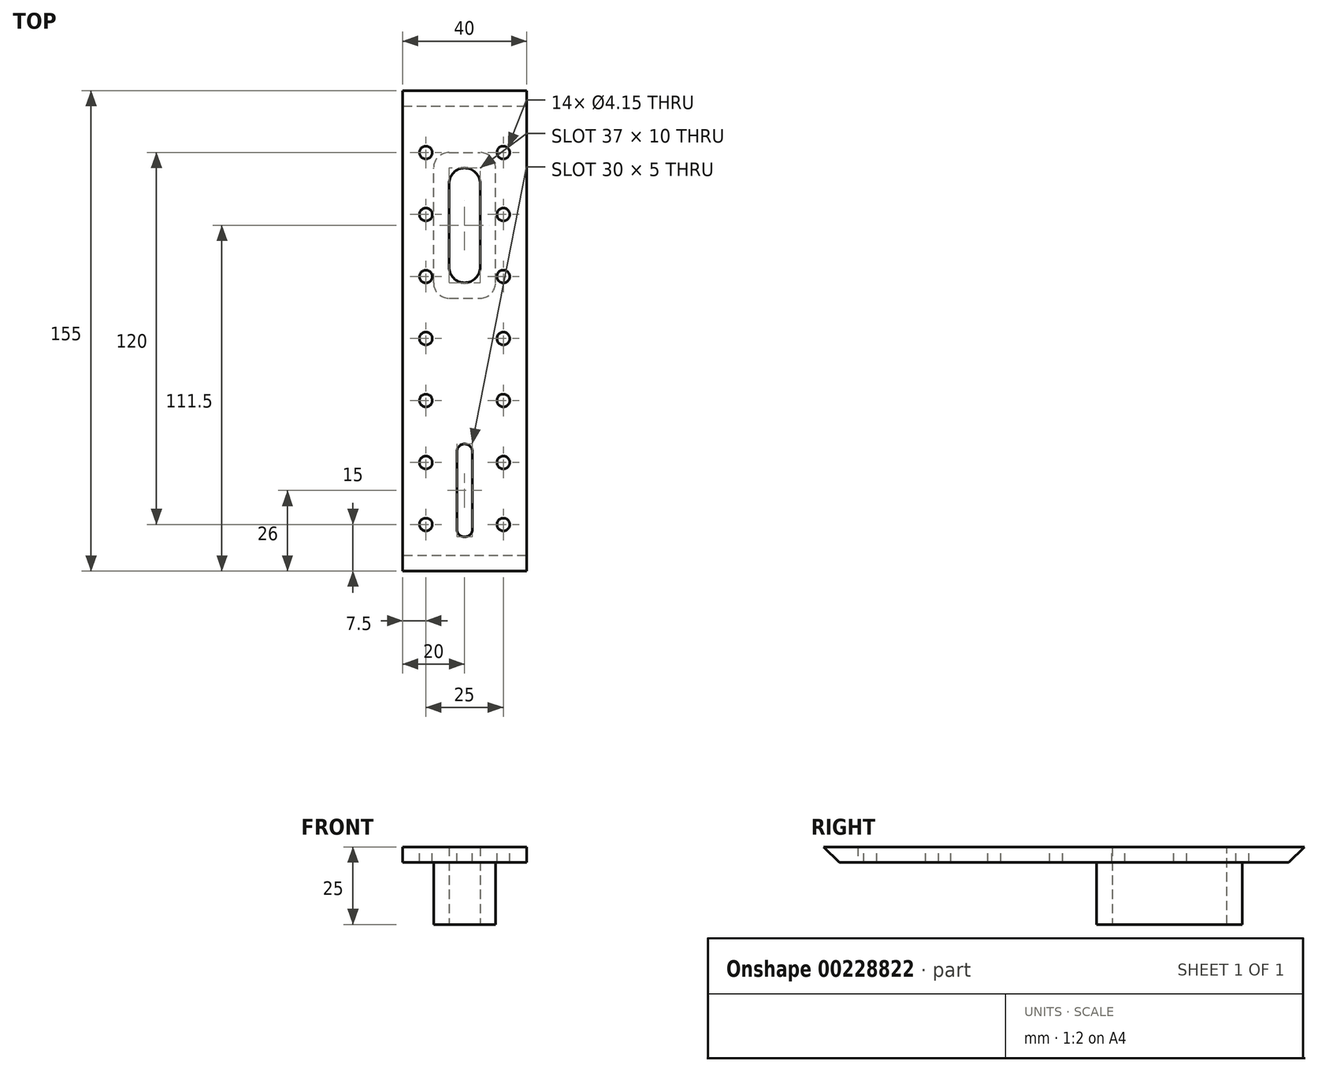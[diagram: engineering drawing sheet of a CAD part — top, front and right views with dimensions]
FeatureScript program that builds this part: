
annotation { "Feature Type Name" : "Feature", "Feature Type Description" : "" }
export const myFeature = defineFeature(function(context is Context, id is Id, definition is map)
    precondition{}
    {
        {
            var Q0;
            Q0=qCreatedBy(makeId("Top.planeOp"),FACE);
            var sketch = newSketch(context, id + "F0", { "sketchPlane" : qUnion([Q0])});
            skLineSegment(sketch, "E0.bottom", {"start": v(-20, 97.5) * mm, "end": v(20, 97.5) * mm});
            skLineSegment(sketch, "E0.top", {"start": v(-20, -57.5) * mm, "end": v(20, -57.5) * mm});
            skLineSegment(sketch, "E0.left", {"start": v(-20, 97.5) * mm, "end": v(-20, -57.5) * mm});
            skLineSegment(sketch, "E0.right", {"start": v(20, 97.5) * mm, "end": v(20, -57.5) * mm});
            skLineSegment(sketch, "E1.bottom", {"start": v(-5, 72.5) * mm, "end": v(5, 72.5) * mm});
            skLineSegment(sketch, "E1.top", {"start": v(-5, 35.5) * mm, "end": v(5, 35.5) * mm});
            skLineSegment(sketch, "E1.left", {"start": v(-5, 72.5) * mm, "end": v(-5, 35.5) * mm});
            skLineSegment(sketch, "E1.right", {"start": v(5, 72.5) * mm, "end": v(5, 35.5) * mm});
            skSolve(sketch);
        }
        {
            var Q0;
            Q0=makeQuery(id+"F0.imprint","IMPRINT",FACE,{"disambiguationData":[TD([[makeQuery(id+"F0.imprint","IMPRINT",EDGE,{"derivedFrom":sQuery(id+"F0.wireOp",EDGE,"E0.bottom")}),-1.0]])]});
            extrude(context, id + "F1", {"entities" : qUnion([Q0]), "depth" : 5 * mm});
        }
        {
            var Q0;
            Q0=makeQuery(id+"F1.opExtrude","SWEPT_EDGE",EDGE,{"disambiguationData":[OSD([sQuery(id+"F0.wireOp",EDGE,"E1.bottom"),sQuery(id+"F0.wireOp",EDGE,"E1.right")])]});
            var Q1;
            Q1=makeQuery(id+"F1.opExtrude","SWEPT_EDGE",EDGE,{"disambiguationData":[OSD([sQuery(id+"F0.wireOp",EDGE,"E1.bottom"),sQuery(id+"F0.wireOp",EDGE,"E1.left")])]});
            var Q2;
            Q2=makeQuery(id+"F1.opExtrude","SWEPT_EDGE",EDGE,{"disambiguationData":[OSD([sQuery(id+"F0.wireOp",EDGE,"E1.top"),sQuery(id+"F0.wireOp",EDGE,"E1.right")])]});
            var Q3;
            Q3=makeQuery(id+"F1.opExtrude","SWEPT_EDGE",EDGE,{"disambiguationData":[OSD([sQuery(id+"F0.wireOp",EDGE,"E1.top"),sQuery(id+"F0.wireOp",EDGE,"E1.left")])]});
            fillet(context, id + "F2", {"entities" : qUnion([Q0, Q1, Q2, Q3]), "radius" : 5 * mm, "tangentPropagation" : true, "allowEdgeOverflow" : false});
        }
        {
            var Q0;
            Q0=makeQuery(id+"F1.opExtrude","CAP_FACE",FACE,{"disambiguationData":[OSD([sQuery(id+"F0.wireOp",EDGE,"E0.bottom"),sQuery(id+"F0.wireOp",EDGE,"E0.top"),sQuery(id+"F0.wireOp",EDGE,"E0.left"),sQuery(id+"F0.wireOp",EDGE,"E0.right"),sQuery(id+"F0.wireOp",EDGE,"E1.bottom"),sQuery(id+"F0.wireOp",EDGE,"E1.top"),sQuery(id+"F0.wireOp",EDGE,"E1.left"),sQuery(id+"F0.wireOp",EDGE,"E1.right")])],"isStart":true});
            var sketch = newSketch(context, id + "F3", { "sketchPlane" : qUnion([Q0])});
            skLineSegment(sketch, "E2.bottom", {"start": v(-10, -30.5) * mm, "end": v(10, -30.5) * mm});
            skLineSegment(sketch, "E2.top", {"start": v(-10, -77.5) * mm, "end": v(10, -77.5) * mm});
            skLineSegment(sketch, "E2.left", {"start": v(-10, -30.5) * mm, "end": v(-10, -77.5) * mm});
            skLineSegment(sketch, "E2.right", {"start": v(10, -30.5) * mm, "end": v(10, -77.5) * mm});
            skSolve(sketch);
        }
        {
            var Q0;
            Q0=makeQuery(id+"F3.imprint","IMPRINT",FACE,{"disambiguationData":[TD([[makeQuery(id+"F3.imprint","IMPRINT",EDGE,{"derivedFrom":sQuery(id+"F3.wireOp",EDGE,"E2.bottom")}),-1.0]])]});
            extrude(context, id + "F4", {"entities" : qUnion([Q0]), "operationType" : NewBodyOperationType.ADD, "depth" : 20 * mm});
        }
        {
            var Q0;
            Q0=makeQuery(id+"F4.opExtrude","SWEPT_EDGE",EDGE,{"disambiguationData":[OSD([sQuery(id+"F3.wireOp",EDGE,"E2.bottom"),sQuery(id+"F3.wireOp",EDGE,"E2.left")])]});
            var Q1;
            Q1=makeQuery(id+"F4.opExtrude","SWEPT_EDGE",EDGE,{"disambiguationData":[OSD([sQuery(id+"F3.wireOp",EDGE,"E2.bottom"),sQuery(id+"F3.wireOp",EDGE,"E2.right")])]});
            var Q2;
            Q2=makeQuery(id+"F4.opExtrude","SWEPT_EDGE",EDGE,{"disambiguationData":[OSD([sQuery(id+"F3.wireOp",EDGE,"E2.top"),sQuery(id+"F3.wireOp",EDGE,"E2.left")])]});
            var Q3;
            Q3=makeQuery(id+"F4.opExtrude","SWEPT_EDGE",EDGE,{"disambiguationData":[OSD([sQuery(id+"F3.wireOp",EDGE,"E2.top"),sQuery(id+"F3.wireOp",EDGE,"E2.right")])]});
            fillet(context, id + "F5", {"entities" : qUnion([Q0, Q1, Q2, Q3]), "radius" : 5 * mm, "tangentPropagation" : true, "allowEdgeOverflow" : false});
        }
        {
            var Q0;
            Q0=makeQuery(id+"F1.opExtrude","CAP_EDGE",EDGE,{"disambiguationData":[OSD([sQuery(id+"F0.wireOp",EDGE,"E0.bottom")])],"isStart":true});
            var Q1;
            Q1=makeQuery(id+"F1.opExtrude","CAP_EDGE",EDGE,{"disambiguationData":[OSD([sQuery(id+"F0.wireOp",EDGE,"E0.top")])],"isStart":true});
            chamfer(context, id + "F6", {"entities" : qUnion([Q0, Q1]), "width" : 5 * mm, "tangentPropagation" : true});
        }
        {
            var Q0;
            Q0=makeQuery(id+"F1.opExtrude","CAP_FACE",FACE,{"disambiguationData":[OSD([sQuery(id+"F0.wireOp",EDGE,"E0.bottom"),sQuery(id+"F0.wireOp",EDGE,"E0.top"),sQuery(id+"F0.wireOp",EDGE,"E0.left"),sQuery(id+"F0.wireOp",EDGE,"E0.right"),sQuery(id+"F0.wireOp",EDGE,"E1.bottom"),sQuery(id+"F0.wireOp",EDGE,"E1.top"),sQuery(id+"F0.wireOp",EDGE,"E1.left"),sQuery(id+"F0.wireOp",EDGE,"E1.right")])],"isStart":false});
            var sketch = newSketch(context, id + "F7", { "sketchPlane" : qUnion([Q0])});
            skCircle(sketch, "E3", {"center": v(-12.5, -42.5) * mm, "radius": 2.07 * mm});
            skCircle(sketch, "E4.0.1.0", {"center": v(-12.5, -22.5) * mm, "radius": 2.07 * mm});
            skCircle(sketch, "E4.0.2.0", {"center": v(-12.5, -2.5) * mm, "radius": 2.07 * mm});
            skCircle(sketch, "E4.0.3.0", {"center": v(-12.5, 17.5) * mm, "radius": 2.07 * mm});
            skCircle(sketch, "E4.0.4.0", {"center": v(-12.5, 37.5) * mm, "radius": 2.07 * mm});
            skCircle(sketch, "E4.1.0.0", {"center": v(12.5, -42.5) * mm, "radius": 2.07 * mm});
            skCircle(sketch, "E4.1.1.0", {"center": v(12.5, -22.5) * mm, "radius": 2.07 * mm});
            skCircle(sketch, "E4.1.2.0", {"center": v(12.5, -2.5) * mm, "radius": 2.07 * mm});
            skCircle(sketch, "E4.1.3.0", {"center": v(12.5, 17.5) * mm, "radius": 2.07 * mm});
            skCircle(sketch, "E4.1.4.0", {"center": v(12.5, 37.5) * mm, "radius": 2.07 * mm});
            skLineSegment(sketch, "E4.direction1", {"start": v(-12.5, -42.5) * mm, "end": v(12.5, -42.5) * mm, "construction": true});
            skLineSegment(sketch, "E4.direction2", {"start": v(-12.5, -42.5) * mm, "end": v(-12.5, -22.5) * mm, "construction": true});
            skCircle(sketch, "E5.0.0.5", {"center": v(-12.5, 57.5) * mm, "radius": 2.07 * mm});
            skCircle(sketch, "E5.0.0.6", {"center": v(-12.5, 77.5) * mm, "radius": 2.07 * mm});
            skCircle(sketch, "E5.0.1.5", {"center": v(12.5, 57.5) * mm, "radius": 2.07 * mm});
            skCircle(sketch, "E5.0.1.6", {"center": v(12.5, 77.5) * mm, "radius": 2.07 * mm});
            skSolve(sketch);
        }
        {
            var Q0;
            Q0=makeQuery(id+"F7.imprint","IMPRINT",FACE,{"disambiguationData":[TD([[makeQuery(id+"F7.imprint","IMPRINT",EDGE,{"derivedFrom":sQuery(id+"F7.wireOp",EDGE,"E3")}),1.0]])]});
            var Q1;
            Q1=makeQuery(id+"F7.imprint","IMPRINT",FACE,{"disambiguationData":[TD([[makeQuery(id+"F7.imprint","IMPRINT",EDGE,{"derivedFrom":sQuery(id+"F7.wireOp",EDGE,"E4.1.0.0")}),1.0]])]});
            var Q2;
            Q2=makeQuery(id+"F7.imprint","IMPRINT",FACE,{"disambiguationData":[TD([[makeQuery(id+"F7.imprint","IMPRINT",EDGE,{"derivedFrom":sQuery(id+"F7.wireOp",EDGE,"E4.0.1.0")}),1.0]])]});
            var Q3;
            Q3=makeQuery(id+"F7.imprint","IMPRINT",FACE,{"disambiguationData":[TD([[makeQuery(id+"F7.imprint","IMPRINT",EDGE,{"derivedFrom":sQuery(id+"F7.wireOp",EDGE,"E4.1.1.0")}),1.0]])]});
            var Q4;
            Q4=makeQuery(id+"F7.imprint","IMPRINT",FACE,{"disambiguationData":[TD([[makeQuery(id+"F7.imprint","IMPRINT",EDGE,{"derivedFrom":sQuery(id+"F7.wireOp",EDGE,"E4.0.2.0")}),1.0]])]});
            var Q5;
            Q5=makeQuery(id+"F7.imprint","IMPRINT",FACE,{"disambiguationData":[TD([[makeQuery(id+"F7.imprint","IMPRINT",EDGE,{"derivedFrom":sQuery(id+"F7.wireOp",EDGE,"E4.1.2.0")}),1.0]])]});
            var Q6;
            Q6=makeQuery(id+"F7.imprint","IMPRINT",FACE,{"disambiguationData":[TD([[makeQuery(id+"F7.imprint","IMPRINT",EDGE,{"derivedFrom":sQuery(id+"F7.wireOp",EDGE,"E4.0.3.0")}),1.0]])]});
            var Q7;
            Q7=makeQuery(id+"F7.imprint","IMPRINT",FACE,{"disambiguationData":[TD([[makeQuery(id+"F7.imprint","IMPRINT",EDGE,{"derivedFrom":sQuery(id+"F7.wireOp",EDGE,"E4.1.3.0")}),1.0]])]});
            var Q8;
            Q8=makeQuery(id+"F7.imprint","IMPRINT",FACE,{"disambiguationData":[TD([[makeQuery(id+"F7.imprint","IMPRINT",EDGE,{"derivedFrom":sQuery(id+"F7.wireOp",EDGE,"E4.0.4.0")}),1.0]])]});
            var Q9;
            Q9=makeQuery(id+"F7.imprint","IMPRINT",FACE,{"disambiguationData":[TD([[makeQuery(id+"F7.imprint","IMPRINT",EDGE,{"derivedFrom":sQuery(id+"F7.wireOp",EDGE,"E4.1.4.0")}),1.0]])]});
            var Q10;
            Q10=makeQuery(id+"F7.imprint","IMPRINT",FACE,{"disambiguationData":[TD([[makeQuery(id+"F7.imprint","IMPRINT",EDGE,{"derivedFrom":sQuery(id+"F7.wireOp",EDGE,"E5.0.1.5")}),1.0]])]});
            var Q11;
            Q11=makeQuery(id+"F7.imprint","IMPRINT",FACE,{"disambiguationData":[TD([[makeQuery(id+"F7.imprint","IMPRINT",EDGE,{"derivedFrom":sQuery(id+"F7.wireOp",EDGE,"E5.0.0.5")}),1.0]])]});
            var Q12;
            Q12=makeQuery(id+"F7.imprint","IMPRINT",FACE,{"disambiguationData":[TD([[makeQuery(id+"F7.imprint","IMPRINT",EDGE,{"derivedFrom":sQuery(id+"F7.wireOp",EDGE,"E5.0.1.6")}),1.0]])]});
            var Q13;
            Q13=makeQuery(id+"F7.imprint","IMPRINT",FACE,{"disambiguationData":[TD([[makeQuery(id+"F7.imprint","IMPRINT",EDGE,{"derivedFrom":sQuery(id+"F7.wireOp",EDGE,"E5.0.0.6")}),1.0]])]});
            extrude(context, id + "F8", {"entities" : qUnion([Q0, Q1, Q2, Q3, Q4, Q5, Q6, Q7, Q8, Q9, Q10, Q11, Q12, Q13]), "operationType" : NewBodyOperationType.REMOVE, "endBound" : BoundingType.THROUGH_ALL, "oppositeDirection" : true, "depth" : 25 * mm});
        }
        {
            var Q0;
            Q0=makeQuery(id+"F1.opExtrude","CAP_FACE",FACE,{"disambiguationData":[OSD([sQuery(id+"F0.wireOp",EDGE,"E0.bottom"),sQuery(id+"F0.wireOp",EDGE,"E0.top"),sQuery(id+"F0.wireOp",EDGE,"E0.left"),sQuery(id+"F0.wireOp",EDGE,"E0.right"),sQuery(id+"F0.wireOp",EDGE,"E1.bottom"),sQuery(id+"F0.wireOp",EDGE,"E1.top"),sQuery(id+"F0.wireOp",EDGE,"E1.left"),sQuery(id+"F0.wireOp",EDGE,"E1.right")])],"isStart":false});
            var sketch = newSketch(context, id + "F9", { "sketchPlane" : qUnion([Q0])});
            skLineSegment(sketch, "E6.bottom", {"start": v(-2.5, -16.5) * mm, "end": v(2.5, -16.5) * mm});
            skLineSegment(sketch, "E6.top", {"start": v(-2.5, -46.5) * mm, "end": v(2.5, -46.5) * mm});
            skLineSegment(sketch, "E6.left", {"start": v(-2.5, -16.5) * mm, "end": v(-2.5, -46.5) * mm});
            skLineSegment(sketch, "E6.right", {"start": v(2.5, -16.5) * mm, "end": v(2.5, -46.5) * mm});
            skSolve(sketch);
        }
        {
            var Q0;
            Q0=makeQuery(id+"F9.imprint","IMPRINT",FACE,{"disambiguationData":[TD([[makeQuery(id+"F9.imprint","IMPRINT",EDGE,{"derivedFrom":sQuery(id+"F9.wireOp",EDGE,"E6.bottom")}),-1.0]])]});
            extrude(context, id + "F10", {"entities" : qUnion([Q0]), "operationType" : NewBodyOperationType.REMOVE, "endBound" : BoundingType.THROUGH_ALL, "oppositeDirection" : true, "depth" : 25 * mm});
        }
        {
            var Q0;
            Q0=makeQuery(id+"F10.boolean.opBoolean","COPY",EDGE,{"derivedFrom":makeQuery(id+"F10.opExtrude","SWEPT_EDGE",EDGE,{"disambiguationData":[OSD([sQuery(id+"F9.wireOp",EDGE,"E6.top"),sQuery(id+"F9.wireOp",EDGE,"E6.left")])]})});
            var Q1;
            Q1=makeQuery(id+"F10.boolean.opBoolean","COPY",EDGE,{"derivedFrom":makeQuery(id+"F10.opExtrude","SWEPT_EDGE",EDGE,{"disambiguationData":[OSD([sQuery(id+"F9.wireOp",EDGE,"E6.top"),sQuery(id+"F9.wireOp",EDGE,"E6.right")])]})});
            var Q2;
            Q2=makeQuery(id+"F10.boolean.opBoolean","COPY",EDGE,{"derivedFrom":makeQuery(id+"F10.opExtrude","SWEPT_EDGE",EDGE,{"disambiguationData":[OSD([sQuery(id+"F9.wireOp",EDGE,"E6.bottom"),sQuery(id+"F9.wireOp",EDGE,"E6.left")])]})});
            var Q3;
            Q3=makeQuery(id+"F10.boolean.opBoolean","COPY",EDGE,{"derivedFrom":makeQuery(id+"F10.opExtrude","SWEPT_EDGE",EDGE,{"disambiguationData":[OSD([sQuery(id+"F9.wireOp",EDGE,"E6.bottom"),sQuery(id+"F9.wireOp",EDGE,"E6.right")])]})});
            fillet(context, id + "F11", {"entities" : qUnion([Q0, Q1, Q2, Q3]), "radius" : 2.5 * mm, "tangentPropagation" : true, "allowEdgeOverflow" : false});
        }
    });
